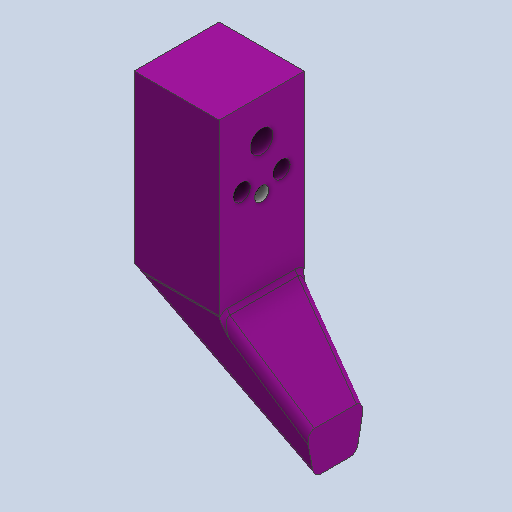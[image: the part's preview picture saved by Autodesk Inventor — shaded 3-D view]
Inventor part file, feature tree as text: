
AUTODESK INVENTOR PART (.ipt)
format: ipt  version: 2025.1 (Build 291241020, 241B)  size: 222,208 bytes
history: native  units: in
note: dims shown in document units (in); Inventor stores cm internally (conversion verified against a paired STEP export)
features: extrude x6, sketch x6, fillet x1
ambient origin geometry x8: Origin, YZ Plane, XZ Plane, XY Plane, X Axis, Y Axis, Z Axis, Center Point
bodies: Solid1 (feature_tree)
feature tree (13):
  extrude  "Extrusion1"  Depth=1.5in
  extrude  "Extrusion2"  Depth=2.0in
  extrude  "Extrusion3"  Depth=1.5in TaperAngle=0.0deg
  fillet  "Fillet1"  Radius=0.375in
  extrude  "Extrusion4"  Depth=1.5in
  extrude  "Extrusion5"  Depth=0.7in
  extrude  "Extrusion6"  Depth=0.125in
  sketch  "Sketch1"  dims[d0=3.0in d1=1.5in]
  sketch  "Sketch3"  dims[d3=2.8in d4=2.0in]
  sketch  "Sketch4"  dims[d5=0.75in d6=1.5in d7=0.0in d9=0.375in]
  sketch  "Sketch5"  dims[d10=1.5in d11=0.0in d12=1.3in]
  sketch  "Sketch6"  dims[d13=0.3976in d14=0.7in]
  sketch  "Sketch7"  dims[d15=1.0in d16=0.0in d17=0.125in d18=0.1875in d19=0.1875in d20=0.4in d21=0.4in d22=1.3in d23=1.0in d24=0.0in d25=0.3in d26=0.1875in d27=0.0in d28=0.25in d29=1.5in d30=0.8in d31=0.6in d32=0.55in d33=0.55in d34=0.055in d35=0.0in]
